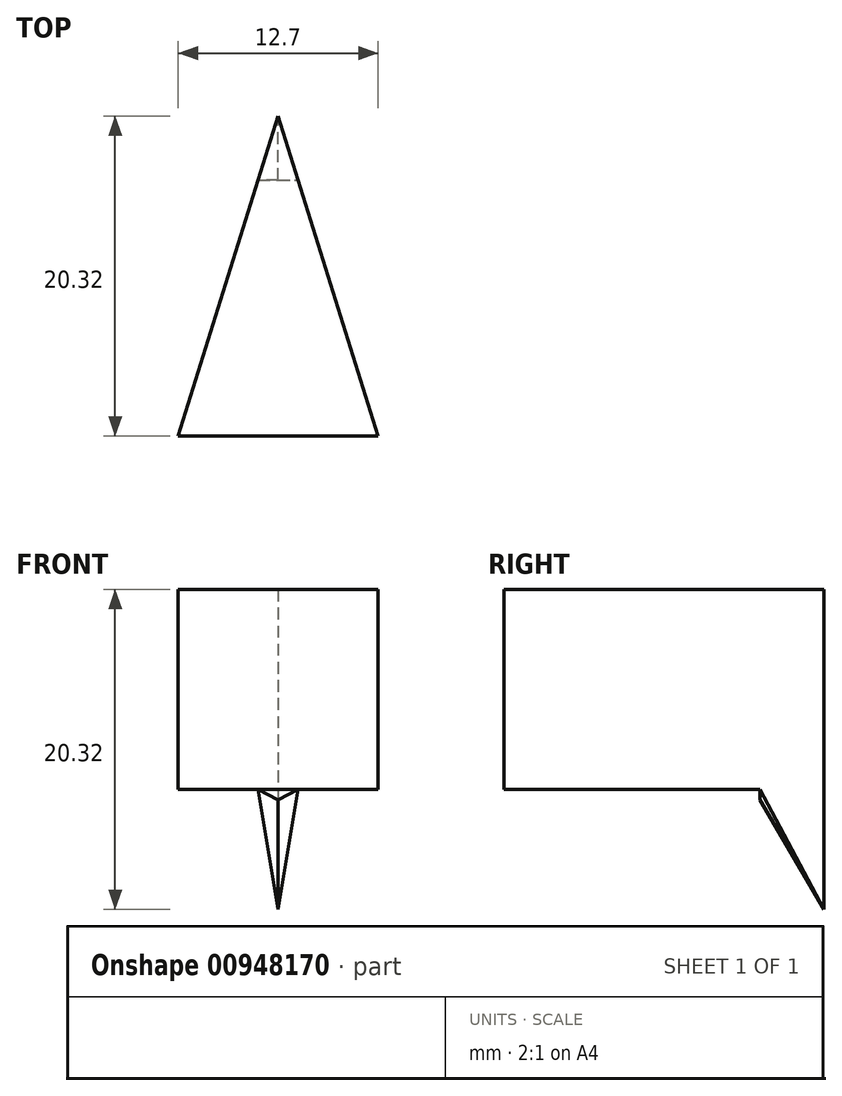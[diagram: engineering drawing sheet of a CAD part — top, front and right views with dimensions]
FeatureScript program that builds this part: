
annotation { "Feature Type Name" : "Feature", "Feature Type Description" : "" }
export const myFeature = defineFeature(function(context is Context, id is Id, definition is map)
    precondition{}
    {
        {
            var Q0;
            Q0=qCreatedBy(makeId("Top.planeOp"),FACE);
            var sketch = newSketch(context, id + "F0", { "sketchPlane" : qUnion([Q0])});
            skLineSegment(sketch, "E0", {"start": v(-5.53, 8.07) * mm, "end": v(7.17, 8.07) * mm});
            skLineSegment(sketch, "E1", {"start": v(0.82, 28.4) * mm, "end": v(-5.53, 8.07) * mm});
            skPoint(sketch, "E1.startSnap0", {"position": v(0.82, 8.07) * mm});
            skLineSegment(sketch, "E2", {"start": v(0.82, 28.4) * mm, "end": v(7.17, 8.07) * mm});
            skSolve(sketch);
        }
        {
            var Q0;
            Q0=makeQuery(id+"F0.imprint","IMPRINT",FACE,{"disambiguationData":[TD([[makeQuery(id+"F0.imprint","IMPRINT",EDGE,{"derivedFrom":sQuery(id+"F0.wireOp",EDGE,"E0")}),1.0]])]});
            extrude(context, id + "F1", {"entities" : qUnion([Q0]), "depth" : 12.7 * mm, "offsetDistance" : 25.4 * mm});
        }
        {
            var Q0;
            Q0=makeQuery(id+"F1.opExtrude","CAP_FACE",FACE,{"disambiguationData":[OSD([sQuery(id+"F0.wireOp",EDGE,"E0"),sQuery(id+"F0.wireOp",EDGE,"E1"),sQuery(id+"F0.wireOp",EDGE,"E2")])],"isStart":true});
            var sketch = newSketch(context, id + "F2", { "sketchPlane" : qUnion([Q0])});
            skLineSegment(sketch, "E3", {"start": v(-0.45, -24.33) * mm, "end": v(2.1, -24.33) * mm});
            skLineSegment(sketch, "E4.bottom", {"start": v(-0.45, -8.07) * mm, "end": v(2.1, -8.07) * mm});
            skLineSegment(sketch, "E4.left", {"start": v(-0.45, -8.07) * mm, "end": v(-0.45, -24.33) * mm});
            skLineSegment(sketch, "E4.right", {"start": v(2.1, -8.07) * mm, "end": v(2.1, -24.33) * mm});
            skSolve(sketch);
        }
        {
            var Q0;
            {var subQ0=sQuery(id+"F2.wireOp",EDGE,"E3");Q0=makeQuery(id+"F2.imprint","IMPRINT",FACE,{"disambiguationData":[TD([[makeQuery(id+"F2.imprint","IMPRINT",EDGE,{"derivedFrom":subQ0}),-1.0]])]});}
            extrude(context, id + "F3", {"entities" : qUnion([Q0]), "operationType" : NewBodyOperationType.ADD, "depth" : 7.62 * mm, "offsetDistance" : 25.4 * mm});
        }
        {
            var Q0;
            {var subQ0=sQuery(id+"F0.wireOp",EDGE,"E1");Q0=makeQuery(id+"F3.boolean.opBoolean","MERGE",FACE,{"derivedFrom":[makeQuery(id+"F1.opExtrude","SWEPT_FACE",FACE,{"disambiguationData":[OSD([subQ0])]}),makeQuery(id+"F3.opExtrude","SWEPT_FACE",FACE,{"disambiguationData":[OSD([subQ0])]})]});}
            var sketch = newSketch(context, id + "F4", { "sketchPlane" : qUnion([Q0])});
            skLineSegment(sketch, "E5", {"start": v(-23.09, 0) * mm, "end": v(-27.34, -7.62) * mm});
            skSolve(sketch);
        }
        {
            var Q0;
            Q0=makeQuery(id+"F4.imprint","IMPRINT",FACE,{"disambiguationData":[TD([[makeQuery(id+"F4.imprint","IMPRINT",EDGE,{"derivedFrom":sQuery(id+"F4.wireOp",EDGE,"E5")}),1.0]])]});
            extrude(context, id + "F5", {"entities" : qUnion([Q0]), "operationType" : NewBodyOperationType.REMOVE, "oppositeDirection" : true, "depth" : 25.4 * mm, "offsetDistance" : 25.4 * mm});
        }
        {
            var Q0;
            {var subQ0=sQuery(id+"F0.wireOp",EDGE,"E2");Q0=makeQuery(id+"F3.boolean.opBoolean","MERGE",FACE,{"derivedFrom":[makeQuery(id+"F1.opExtrude","SWEPT_FACE",FACE,{"disambiguationData":[OSD([subQ0])]}),makeQuery(id+"F3.opExtrude","SWEPT_FACE",FACE,{"disambiguationData":[OSD([subQ0])]})]});}
            var sketch = newSketch(context, id + "F6", { "sketchPlane" : qUnion([Q0])});
            skLineSegment(sketch, "E6", {"start": v(22.6, 0) * mm, "end": v(26.85, -7.62) * mm});
            skSolve(sketch);
        }
        {
            var Q0;
            Q0=makeQuery(id+"F6.imprint","IMPRINT",FACE,{"disambiguationData":[TD([[makeQuery(id+"F6.imprint","IMPRINT",EDGE,{"derivedFrom":sQuery(id+"F6.wireOp",EDGE,"E6")}),-1.0]])]});
            extrude(context, id + "F7", {"entities" : qUnion([Q0]), "operationType" : NewBodyOperationType.REMOVE, "oppositeDirection" : true, "depth" : 25.4 * mm, "offsetDistance" : 25.4 * mm});
        }
    });
